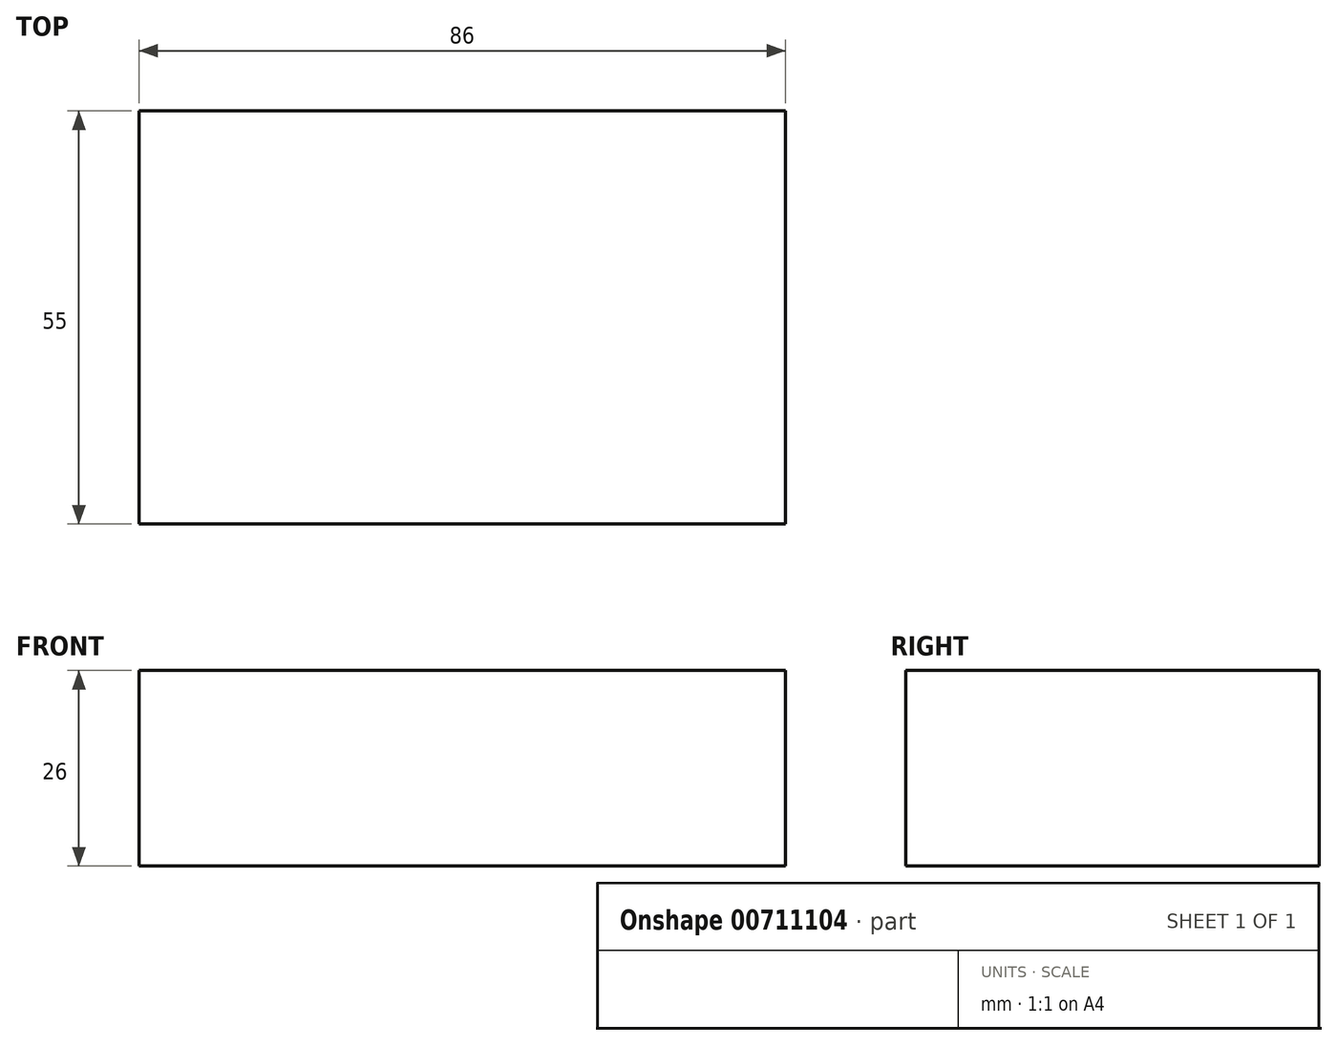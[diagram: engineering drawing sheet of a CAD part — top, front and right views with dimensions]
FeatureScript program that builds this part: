
annotation { "Feature Type Name" : "Feature", "Feature Type Description" : "" }
export const myFeature = defineFeature(function(context is Context, id is Id, definition is map)
    precondition{}
    {
        {
            var Q0;
            Q0=qCreatedBy(makeId("Top.planeOp"),FACE);
            var sketch = newSketch(context, id + "F0", { "sketchPlane" : qUnion([Q0])});
            skLineSegment(sketch, "E0.bottom", {"start": v(-46.45, 75.58) * mm, "end": v(39.55, 75.58) * mm});
            skLineSegment(sketch, "E0.top", {"start": v(-46.45, 20.58) * mm, "end": v(39.55, 20.58) * mm});
            skLineSegment(sketch, "E0.left", {"start": v(-46.45, 75.58) * mm, "end": v(-46.45, 20.58) * mm});
            skLineSegment(sketch, "E0.right", {"start": v(39.55, 75.58) * mm, "end": v(39.55, 20.58) * mm});
            skSolve(sketch);
        }
        {
            var Q0;
            Q0=makeQuery(id+"F0.imprint","IMPRINT",FACE,{"disambiguationData":[TD([[makeQuery(id+"F0.imprint","IMPRINT",EDGE,{"derivedFrom":sQuery(id+"F0.wireOp",EDGE,"E0.bottom")}),-1.0]])]});
            extrude(context, id + "F1", {"entities" : qUnion([Q0]), "depth" : 26 * mm, "offsetDistance" : 25 * mm});
        }
    });
